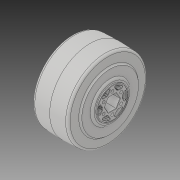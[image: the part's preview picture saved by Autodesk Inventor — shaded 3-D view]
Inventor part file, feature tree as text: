
AUTODESK INVENTOR PART (.ipt)
format: ipt  version: 2019 (Build 230136000, 136)  size: 1,188,864 bytes
history: native  units: in
note: dims shown in document units (in); Inventor stores cm internally (conversion verified against a paired STEP export)
features: revolve x1
ambient origin geometry x8: Origin, YZ Plane, XZ Plane, XY Plane, X Axis, Y Axis, Z Axis, Center Point
bodies: Solid1 (feature_tree)
feature tree (1):
  revolve  "Revolve1"  [1 undecoded]
note: 1 required parameter value undecoded (feature->parameter linkage not recoverable at this tier; creation-order binding heuristic only, values carry confidence <= 0.55)
